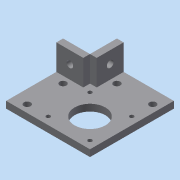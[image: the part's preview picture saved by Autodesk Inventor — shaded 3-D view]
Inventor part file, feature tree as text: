
AUTODESK INVENTOR PART (.ipt)
format: ipt  version: 2015 (Build 190159000, 159)  size: 148,992 bytes
history: native  units: mm
features: sketch x4, hole x4, extrude x2
ambient origin geometry x8: Origin, YZ Plane, XZ Plane, XY Plane, X Axis, Y Axis, Z Axis, Center Point
bodies: Solid1 (feature_tree)
feature tree (10):
  sketch  "Sketch1"  dims[d0=42.3mm d1=23.0mm]
  extrude  "Extrusion1"  Depth=42.3mm
  hole  "Hole1"  [1 undecoded]
  hole  "Hole2"  [1 undecoded]
  extrude  "Extrusion2"  Depth=42.3mm
  hole  "Hole3"  [1 undecoded]
  hole  "Hole4"  [1 undecoded]
  sketch  "Sketch3"  dims[d2=31.0mm d3=31.0mm]
  sketch  "Sketch4"  dims[d4=31.0mm d8=31.0mm]
  sketch  "Sketch5"  dims[d12=21.15mm d16=42.3mm d17=5.65mm d18=5.65mm d19=5.65mm d20=5.65mm d21=20.0mm d22=20.0mm d23=5.0mm d24=0.0mm d25=3.0mm d26=6.0mm d27=4.0mm d28=2.0mm d29=90.0deg d30=8.0mm d31=20.594885mm d32=5.0mm d33=6.0mm d34=4.0mm d35=2.0mm d36=90.0deg d37=8.0mm d38=20.594885mm d39=21.15mm d40=5.0mm d41=5.0mm d42=10.0mm d43=10.0mm d44=19.0mm d45=0.0mm d46=10.0mm d47=10.0mm d50=5.0mm d51=6.0mm d52=4.0mm d53=2.0mm d54=90.0deg d55=8.0mm d56=20.594885mm d58=10.0mm d59=10.0mm d61=5.0mm d62=6.0mm d63=4.0mm d64=2.0mm d65=90.0deg d66=8.0mm d67=20.594885mm]
note: 4 required parameter values undecoded (feature->parameter linkage not recoverable at this tier; creation-order binding heuristic only, values carry confidence <= 0.55)
